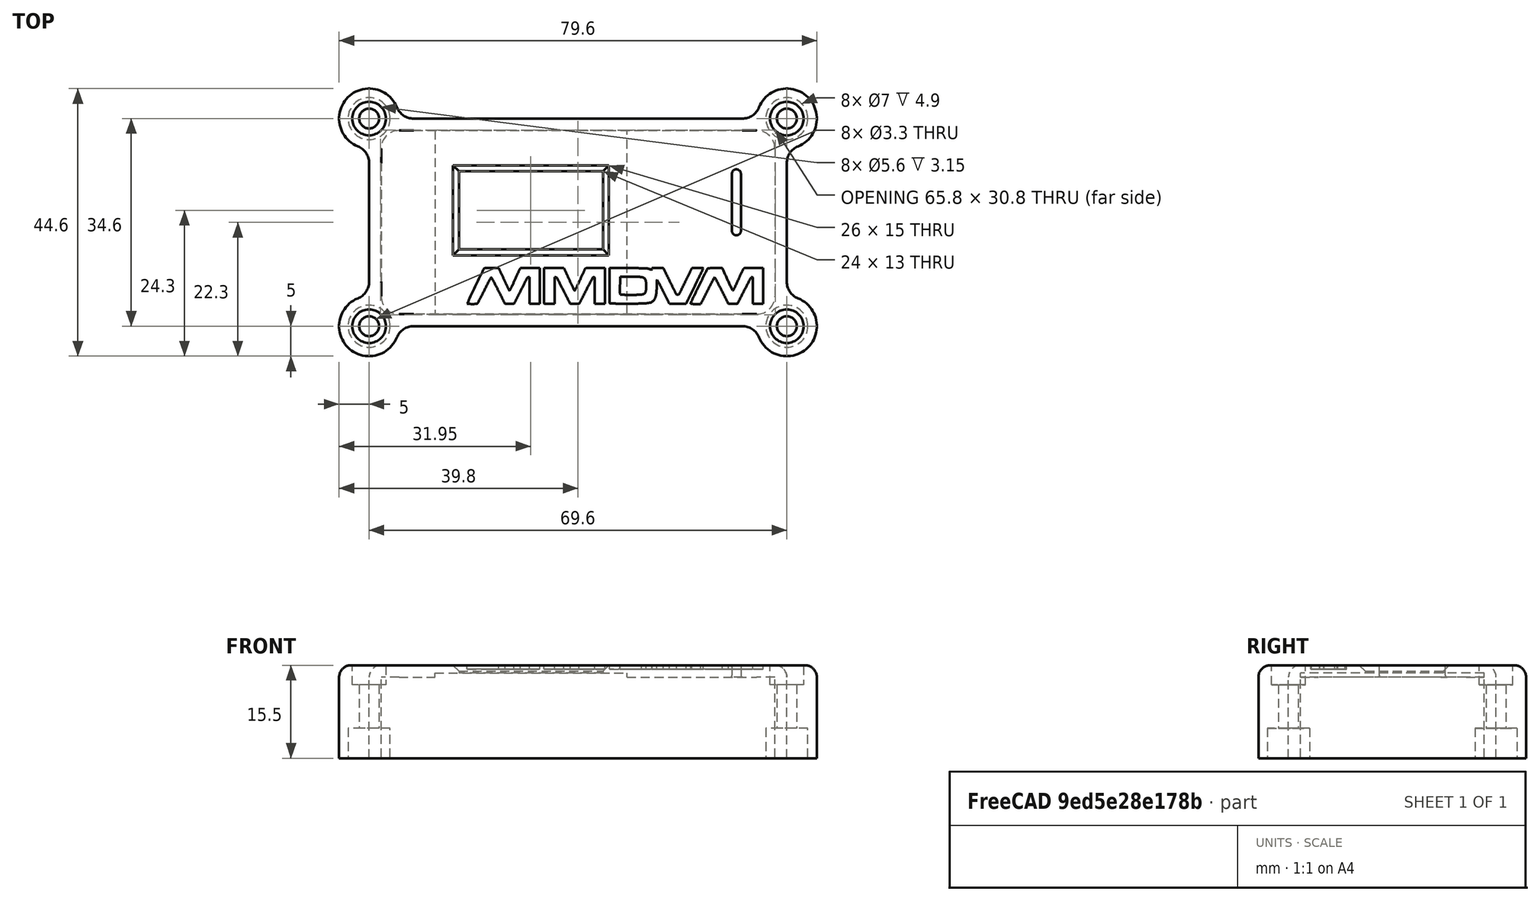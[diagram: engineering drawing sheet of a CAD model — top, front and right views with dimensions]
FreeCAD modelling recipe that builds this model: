
FCSTD DOCUMENT  (FreeCAD 0.18R13830 (Git))
Label: MMDVM_HS_Top-Screen-PCB-v1.2
License: CreativeCommons Attribution-NonCommercial-ShareAlike
LicenseURL: http://creativecommons.org/licenses/by-nc-sa/4.0/
objects: Sketcher::SketchObject×10, PartDesign::Pocket×6, Part::Feature×5, PartDesign::Fillet×4, Part::Cut×2, PartDesign::Pad×1, PartDesign::Chamfer×1, PartDesign::Hole×1, Part::MultiFuse×1, Part::FeaturePython×1, PartDesign::Body×1, Part::Extrusion×1, Mesh::Feature×1
note: 42 computed .brp shape members not serialized (recipe doc carries the construction recipe); baked Part::Feature solids carry a one-line shape summary decoded from their .brp

FEATURE [Sketcher::SketchObject] Sketch
  MapMode = 5
  Support = -> [XY_Plane]
  sketch-geometry (24):
    g0: LineSegment [constr] StartX=-32.5 StartY=15 StartZ=0 EndX=32.5 EndY=15 EndZ=0
    g1: LineSegment [constr] StartX=32.5 StartY=15 StartZ=0 EndX=32.5 EndY=-15 EndZ=0
    g2: LineSegment [constr] StartX=32.5 StartY=-15 StartZ=0 EndX=-32.5 EndY=-15 EndZ=0
    g3: LineSegment [constr] StartX=-32.5 StartY=-15 StartZ=0 EndX=-32.5 EndY=15 EndZ=0
    g4: LineSegment [constr] StartX=-29 StartY=11.5 StartZ=0 EndX=29 EndY=11.5 EndZ=0
    g5: LineSegment [constr] StartX=29 StartY=11.5 StartZ=0 EndX=29 EndY=-11.5 EndZ=0
    g6: LineSegment [constr] StartX=29 StartY=-11.5 StartZ=0 EndX=-29 EndY=-11.5 EndZ=0
    g7: LineSegment [constr] StartX=-29 StartY=-11.5 StartZ=0 EndX=-29 EndY=11.5 EndZ=0
    g8: Circle CenterX=-29 CenterY=11.5 CenterZ=0 NormalX=0 NormalY=0 NormalZ=1 AngleXU=0 Radius=1.375
    g9: Circle CenterX=29 CenterY=11.5 CenterZ=0 NormalX=0 NormalY=0 NormalZ=1 AngleXU=0 Radius=1.375
    g10: Circle CenterX=29 CenterY=-11.5 CenterZ=0 NormalX=0 NormalY=0 NormalZ=1 AngleXU=0 Radius=1.375
    g11: Circle CenterX=-29 CenterY=-11.5 CenterZ=0 NormalX=0 NormalY=0 NormalZ=1 AngleXU=0 Radius=1.375
    g12: LineSegment [constr] StartX=-29.5 StartY=12 StartZ=0 EndX=29.5 EndY=12 EndZ=0
    g13: LineSegment [constr] StartX=29.5 StartY=12 StartZ=0 EndX=29.5 EndY=-12 EndZ=0
    g14: LineSegment [constr] StartX=29.5 StartY=-12 StartZ=0 EndX=-29.5 EndY=-12 EndZ=0
    g15: LineSegment [constr] StartX=-29.5 StartY=-12 StartZ=0 EndX=-29.5 EndY=12 EndZ=0
    g16: ArcOfCircle CenterX=-29.5 CenterY=12 CenterZ=0 NormalX=0 NormalY=0 NormalZ=1 AngleXU=0 Radius=3 StartAngle=1.5708 EndAngle=3.1416
    g17: ArcOfCircle CenterX=29.5 CenterY=12 CenterZ=0 NormalX=0 NormalY=0 NormalZ=1 AngleXU=0 Radius=3 StartAngle=1.42077e-07 EndAngle=1.5708
    g18: ArcOfCircle CenterX=29.5 CenterY=-12 CenterZ=0 NormalX=0 NormalY=0 NormalZ=1 AngleXU=0 Radius=3 StartAngle=4.71239 EndAngle=6.28319
    g19: ArcOfCircle CenterX=-29.5 CenterY=-12 CenterZ=0 NormalX=0 NormalY=0 NormalZ=1 AngleXU=0 Radius=3 StartAngle=3.14159 EndAngle=4.71239
    g20: LineSegment StartX=-29.5 StartY=15 StartZ=0 EndX=29.5 EndY=15 EndZ=0
    g21: LineSegment StartX=32.5 StartY=12 StartZ=0 EndX=32.5 EndY=-12 EndZ=0
    g22: LineSegment StartX=29.5 StartY=-15 StartZ=0 EndX=-29.5 EndY=-15 EndZ=0
    g23: LineSegment StartX=-32.5 StartY=-12 StartZ=0 EndX=-32.5 EndY=12 EndZ=0
  constraints (68):
    c: Coincident(g0,g1)
    c: Coincident(g1,g2)
    c: Coincident(g2,g3)
    c: Coincident(g3,g0)
    c: Horizontal(g0)
    c: Horizontal(g2)
    c: Vertical(g1)
    c: Vertical(g3)
    c: DistanceX(g0,g0) = 65
    c: DistanceY(g1,g1) = 30
    c: Symmetric(g0,g0,g-2)
    c: Symmetric(g0,g1,g-1)
    c: Coincident(g4,g5)
    c: Coincident(g5,g6)
    c: Coincident(g6,g7)
    c: Coincident(g7,g4)
    c: Horizontal(g4)
    c: Horizontal(g6)
    c: Vertical(g5)
    c: Vertical(g7)
    c: DistanceX(g4,g4) = 58
    c: DistanceY(g5,g5) = 23
    c: Symmetric(g4,g5,g-1)
    c: Symmetric(g4,g4,g-2)
    c: Coincident(g8,g4)
    c: Coincident(g9,g4)
    c: Coincident(g10,g5)
    c: Coincident(g11,g6)
    c: Radius(g11) = 1.375
    c: Radius(g8) = 1.375
    c: Radius(g9) = 1.375
    c: Radius(g10) = 1.375
    c: Coincident(g12,g13)
    c: Coincident(g13,g14)
    c: Coincident(g14,g15)
    c: Coincident(g15,g12)
    c: Horizontal(g12)
    c: Horizontal(g14)
    c: Vertical(g13)
    c: Vertical(g15)
    c: DistanceX(g4,g12) = 0.5
    c: DistanceY(g4,g12) = 0.5
    c: DistanceY(g13,g5) = 0.5
    c: DistanceX(g14,g6) = 0.5
    c: Coincident(g16,g12)
    c: Radius(g16) = 3
    c: Coincident(g17,g12)
    c: Radius(g17) = 3
    c: Coincident(g18,g13)
    c: Radius(g18) = 3
    c: Coincident(g19,g14)
    c: Radius(g19) = 3
    c: PointOnObject(g16,g0)
    c: PointOnObject(g17,g1)
    c: PointOnObject(g18,g2)
    c: PointOnObject(g19,g3)
    c: Coincident(g20,g16)
    c: Horizontal(g20)
    c: Coincident(g20,g17)
    c: Coincident(g21,g17)
    c: Vertical(g21)
    c: Coincident(g18,g21)
    c: Coincident(g22,g18)
    c: Horizontal(g22)
    c: Coincident(g19,g22)
    c: Coincident(g23,g19)
    c: Vertical(g23)
    c: Coincident(g23,g16)
FEATURE [Sketcher::SketchObject] Sketch001
  MapMode = 5
  Support = -> [XY_Plane]
  expr: Constraints[8] = Sketch.Constraints[8]
  expr: Constraints[41] = Sketch.Constraints[41]
  expr: Constraints[9] = Sketch.Constraints[9]
  expr: Constraints[45] = Sketch.Constraints[45]
  expr: Constraints[43] = Sketch.Constraints[43]
  expr: Constraints[42] = Sketch.Constraints[42]
  expr: Constraints[20] = Sketch.Constraints[20]
  expr: Constraints[21] = Sketch.Constraints[21]
  expr: Constraints[28] = Sketch.Constraints[28]
  expr: Constraints[29] = Sketch.Constraints[29]
  expr: Constraints[30] = Sketch.Constraints[30]
  expr: Constraints[40] = Sketch.Constraints[40]
  expr: Constraints[31] = Sketch.Constraints[31]
  expr: Constraints[47] = Sketch.Constraints[47]
  expr: Constraints[49] = Sketch.Constraints[49]
  expr: Constraints[51] = Sketch.Constraints[51]
  sketch-geometry (64):
    g0: LineSegment [constr] StartX=-32.5 StartY=15 StartZ=0 EndX=32.5 EndY=15 EndZ=0
    g1: LineSegment [constr] StartX=32.5 StartY=15 StartZ=0 EndX=32.5 EndY=-15 EndZ=0
    g2: LineSegment [constr] StartX=32.5 StartY=-15 StartZ=0 EndX=-32.5 EndY=-15 EndZ=0
    g3: LineSegment [constr] StartX=-32.5 StartY=-15 StartZ=0 EndX=-32.5 EndY=15 EndZ=0
    g4: LineSegment [constr] StartX=-29 StartY=11.5 StartZ=0 EndX=29 EndY=11.5 EndZ=0
    g5: LineSegment [constr] StartX=29 StartY=11.5 StartZ=0 EndX=29 EndY=-11.5 EndZ=0
    g6: LineSegment [constr] StartX=29 StartY=-11.5 StartZ=0 EndX=-29 EndY=-11.5 EndZ=0
    g7: LineSegment [constr] StartX=-29 StartY=-11.5 StartZ=0 EndX=-29 EndY=11.5 EndZ=0
    g8: Circle [constr] CenterX=-29 CenterY=11.5 CenterZ=0 NormalX=0 NormalY=0 NormalZ=1 AngleXU=0 Radius=1.375
    g9: Circle [constr] CenterX=29 CenterY=11.5 CenterZ=0 NormalX=0 NormalY=0 NormalZ=1 AngleXU=0 Radius=1.375
    g10: Circle [constr] CenterX=29 CenterY=-11.5 CenterZ=0 NormalX=0 NormalY=0 NormalZ=1 AngleXU=0 Radius=1.375
    g11: Circle [constr] CenterX=-29 CenterY=-11.5 CenterZ=0 NormalX=0 NormalY=0 NormalZ=1 AngleXU=0 Radius=1.375
    g12: LineSegment [constr] StartX=-29.5 StartY=12 StartZ=0 EndX=29.5 EndY=12 EndZ=0
    g13: LineSegment [constr] StartX=29.5 StartY=12 StartZ=0 EndX=29.5 EndY=-12 EndZ=0
    g14: LineSegment [constr] StartX=29.5 StartY=-12 StartZ=0 EndX=-29.5 EndY=-12 EndZ=0
    g15: LineSegment [constr] StartX=-29.5 StartY=-12 StartZ=0 EndX=-29.5 EndY=12 EndZ=0
    g16: ArcOfCircle [constr] CenterX=-29.5 CenterY=12 CenterZ=0 NormalX=0 NormalY=0 NormalZ=1 AngleXU=0 Radius=3 StartAngle=1.5708 EndAngle=3.14159
    g17: ArcOfCircle [constr] CenterX=29.5 CenterY=12 CenterZ=0 NormalX=0 NormalY=0 NormalZ=1 AngleXU=0 Radius=3 StartAngle=2.8425e-08 EndAngle=1.5708
    g18: ArcOfCircle [constr] CenterX=29.5 CenterY=-12 CenterZ=0 NormalX=0 NormalY=0 NormalZ=1 AngleXU=0 Radius=3 StartAngle=4.71239 EndAngle=6.28319
    g19: ArcOfCircle [constr] CenterX=-29.5 CenterY=-12 CenterZ=0 NormalX=0 NormalY=0 NormalZ=1 AngleXU=0 Radius=3 StartAngle=3.14159 EndAngle=4.71239
    g20: LineSegment [constr] StartX=-29.5 StartY=15 StartZ=0 EndX=29.5 EndY=15 EndZ=0
    g21: LineSegment [constr] StartX=32.5 StartY=12 StartZ=0 EndX=32.5 EndY=-12 EndZ=0
    g22: LineSegment [constr] StartX=29.5 StartY=-15 StartZ=0 EndX=-29.5 EndY=-15 EndZ=0
    g23: LineSegment [constr] StartX=-32.5 StartY=-12 StartZ=0 EndX=-32.5 EndY=12 EndZ=0
    g24: ArcOfCircle [constr] CenterX=-29.5 CenterY=12 CenterZ=0 NormalX=0 NormalY=0 NormalZ=1 AngleXU=0 Radius=3.3 StartAngle=1.5708 EndAngle=3.14159
    g25: ArcOfCircle [constr] CenterX=29.5 CenterY=12 CenterZ=0 NormalX=0 NormalY=0 NormalZ=1 AngleXU=0 Radius=3.3 StartAngle=-2.2e-10 EndAngle=1.5708
    g26: ArcOfCircle [constr] CenterX=29.5 CenterY=-12 CenterZ=0 NormalX=0 NormalY=0 NormalZ=1 AngleXU=0 Radius=3.3 StartAngle=4.71239 EndAngle=6.28319
    g27: ArcOfCircle [constr] CenterX=-29.5 CenterY=-12 CenterZ=0 NormalX=0 NormalY=0 NormalZ=1 AngleXU=0 Radius=3.3 StartAngle=3.14159 EndAngle=4.71239
    g28: LineSegment [constr] StartX=-32.8 StartY=12 StartZ=0 EndX=-32.8 EndY=-12 EndZ=0
    g29: LineSegment [constr] StartX=-29.5 StartY=15.3 StartZ=0 EndX=29.5 EndY=15.3 EndZ=0
    g30: LineSegment [constr] StartX=32.8 StartY=12 StartZ=0 EndX=32.8 EndY=-12 EndZ=0
    g31: LineSegment [constr] StartX=29.5 StartY=-15.3 StartZ=0 EndX=-29.5 EndY=-15.3 EndZ=0
    g32: LineSegment [constr] StartX=-34.8 StartY=17.3 StartZ=0 EndX=34.8 EndY=17.3 EndZ=0
    g33: LineSegment [constr] StartX=34.8 StartY=17.3 StartZ=0 EndX=34.8 EndY=-17.3 EndZ=0
    g34: LineSegment [constr] StartX=34.8 StartY=-17.3 StartZ=0 EndX=-34.8 EndY=-17.3 EndZ=0
    g35: LineSegment [constr] StartX=-34.8 StartY=-17.3 StartZ=0 EndX=-34.8 EndY=17.3 EndZ=0
    g36: Circle [constr] CenterX=34.8 CenterY=17.3 CenterZ=0 NormalX=0 NormalY=0 NormalZ=1 AngleXU=0 Radius=5
    g37: Circle [constr] CenterX=34.8 CenterY=-17.3 CenterZ=0 NormalX=0 NormalY=0 NormalZ=1 AngleXU=0 Radius=5
    g38: Circle [constr] CenterX=-34.8 CenterY=-17.3 CenterZ=0 NormalX=0 NormalY=0 NormalZ=1 AngleXU=0 Radius=5
    g39: Circle [constr] CenterX=-34.8 CenterY=17.3 CenterZ=0 NormalX=0 NormalY=0 NormalZ=1 AngleXU=0 Radius=5
    g40: Circle [constr] CenterX=27.3838 CenterY=20.3 CenterZ=0 NormalX=0 NormalY=0 NormalZ=1 AngleXU=0 Radius=3
    g41: Circle [constr] CenterX=-27.3838 CenterY=20.3 CenterZ=0 NormalX=0 NormalY=0 NormalZ=1 AngleXU=0 Radius=3
    g42: Circle [constr] CenterX=-37.8 CenterY=9.8838 CenterZ=0 NormalX=0 NormalY=0 NormalZ=1 AngleXU=0 Radius=3
    g43: Circle [constr] CenterX=-37.8 CenterY=-9.8838 CenterZ=0 NormalX=0 NormalY=0 NormalZ=1 AngleXU=0 Radius=3
    g44: Circle [constr] CenterX=-27.3838 CenterY=-20.3 CenterZ=0 NormalX=0 NormalY=0 NormalZ=1 AngleXU=0 Radius=3
    g45: Circle [constr] CenterX=27.3838 CenterY=-20.3 CenterZ=0 NormalX=0 NormalY=0 NormalZ=1 AngleXU=0 Radius=3
    g46: Circle [constr] CenterX=37.8 CenterY=-9.8838 CenterZ=0 NormalX=0 NormalY=0 NormalZ=1 AngleXU=0 Radius=3
    g47: Circle [constr] CenterX=37.8 CenterY=9.8838 CenterZ=0 NormalX=0 NormalY=0 NormalZ=1 AngleXU=0 Radius=3
    g48: ArcOfCircle CenterX=34.8 CenterY=17.3 CenterZ=0 NormalX=0 NormalY=0 NormalZ=1 AngleXU=0 Radius=5 StartAngle=5.09679 EndAngle=9.04038
    g49: ArcOfCircle CenterX=27.3838 CenterY=20.3 CenterZ=0 NormalX=0 NormalY=0 NormalZ=1 AngleXU=0 Radius=3 StartAngle=4.71239 EndAngle=5.89879
    g50: ArcOfCircle CenterX=37.8 CenterY=9.8838 CenterZ=0 NormalX=0 NormalY=0 NormalZ=1 AngleXU=0 Radius=3 StartAngle=1.95519 EndAngle=3.14159
    g51: ArcOfCircle CenterX=37.8 CenterY=-9.8838 CenterZ=0 NormalX=0 NormalY=0 NormalZ=1 AngleXU=0 Radius=3 StartAngle=3.14159 EndAngle=4.32799
    g52: ArcOfCircle CenterX=34.8 CenterY=-17.3 CenterZ=0 NormalX=0 NormalY=0 NormalZ=1 AngleXU=0 Radius=5 StartAngle=3.52599 EndAngle=7.46958
    g53: ArcOfCircle CenterX=27.3838 CenterY=-20.3 CenterZ=0 NormalX=0 NormalY=0 NormalZ=1 AngleXU=0 Radius=3 StartAngle=0.384397 EndAngle=1.5708
    g54: ArcOfCircle CenterX=-27.3838 CenterY=-20.3 CenterZ=0 NormalX=0 NormalY=0 NormalZ=1 AngleXU=0 Radius=3 StartAngle=1.5708 EndAngle=2.7572
    g55: ArcOfCircle CenterX=-34.8 CenterY=-17.3 CenterZ=0 NormalX=0 NormalY=0 NormalZ=1 AngleXU=0 Radius=5 StartAngle=1.95519 EndAngle=5.89879
    g56: ArcOfCircle CenterX=-37.8 CenterY=-9.8838 CenterZ=0 NormalX=0 NormalY=0 NormalZ=1 AngleXU=0 Radius=3 StartAngle=5.09679 EndAngle=6.28319
    g57: ArcOfCircle CenterX=-37.8 CenterY=9.8838 CenterZ=0 NormalX=0 NormalY=0 NormalZ=1 AngleXU=0 Radius=3 StartAngle=6.28319 EndAngle=7.46958
    g58: ArcOfCircle CenterX=-34.8 CenterY=17.3 CenterZ=0 NormalX=0 NormalY=0 NormalZ=1 AngleXU=0 Radius=5 StartAngle=0.384397 EndAngle=4.32799
    g59: ArcOfCircle CenterX=-27.3838 CenterY=20.3 CenterZ=0 NormalX=0 NormalY=0 NormalZ=1 AngleXU=0 Radius=3 StartAngle=3.52599 EndAngle=4.71239
    g60: LineSegment StartX=-27.3838 StartY=17.3 StartZ=0 EndX=27.3838 EndY=17.3 EndZ=0
    g61: LineSegment StartX=34.8 StartY=9.8838 StartZ=0 EndX=34.8 EndY=-9.8838 EndZ=0
    g62: LineSegment StartX=27.3838 StartY=-17.3 StartZ=0 EndX=-27.3838 EndY=-17.3 EndZ=0
    g63: LineSegment StartX=-34.8 StartY=-9.8838 StartZ=0 EndX=-34.8 EndY=9.8838 EndZ=0
  constraints (184):
    c: Coincident(g0,g1)
    c: Coincident(g1,g2)
    c: Coincident(g2,g3)
    c: Coincident(g3,g0)
    c: Horizontal(g0)
    c: Horizontal(g2)
    c: Vertical(g1)
    c: Vertical(g3)
    c: DistanceX(g0,g0) = 65
    c: DistanceY(g1,g1) = 30
    c: Symmetric(g0,g0,g-2)
    c: Symmetric(g0,g1,g-1)
    c: Coincident(g4,g5)
    c: Coincident(g5,g6)
    c: Coincident(g6,g7)
    c: Coincident(g7,g4)
    c: Horizontal(g4)
    c: Horizontal(g6)
    c: Vertical(g5)
    c: Vertical(g7)
    c: DistanceX(g4,g4) = 58
    c: DistanceY(g5,g5) = 23
    c: Symmetric(g4,g5,g-1)
    c: Symmetric(g4,g4,g-2)
    c: Coincident(g8,g4)
    c: Coincident(g9,g4)
    c: Coincident(g10,g5)
    c: Coincident(g11,g6)
    c: Radius(g11) = 1.375
    c: Radius(g8) = 1.375
    c: Radius(g9) = 1.375
    c: Radius(g10) = 1.375
    c: Coincident(g12,g13)
    c: Coincident(g13,g14)
    c: Coincident(g14,g15)
    c: Coincident(g15,g12)
    c: Horizontal(g12)
    c: Horizontal(g14)
    c: Vertical(g13)
    c: Vertical(g15)
    c: DistanceX(g4,g12) = 0.5
    c: DistanceY(g4,g12) = 0.5
    c: DistanceY(g13,g5) = 0.5
    c: DistanceX(g14,g6) = 0.5
    c: Coincident(g16,g12)
    c: Radius(g16) = 3
    c: Coincident(g17,g12)
    c: Radius(g17) = 3
    c: Coincident(g18,g13)
    c: Radius(g18) = 3
    c: Coincident(g19,g14)
    c: Radius(g19) = 3
    c: PointOnObject(g16,g0)
    c: PointOnObject(g17,g1)
    c: PointOnObject(g18,g2)
    c: PointOnObject(g19,g3)
    c: Coincident(g20,g16)
    c: Horizontal(g20)
    c: Coincident(g20,g17)
    c: Coincident(g21,g17)
    c: Vertical(g21)
    c: Coincident(g18,g21)
    c: Coincident(g22,g18)
    c: Horizontal(g22)
    c: Coincident(g19,g22)
    c: Coincident(g23,g19)
    c: Vertical(g23)
    c: Coincident(g23,g16)
    c: Coincident(g24,g12)
    c: Radius(g24) = 3.3
    c: Coincident(g25,g12)
    c: Radius(g25) = 3.3
    c: Coincident(g26,g13)
    c: Radius(g26) = 3.3
    c: Coincident(g27,g14)
    c: Radius(g27) = 3.3
    c: Vertical(g28)
    c: DistanceX(g28,g2) = 0.3
    c: Coincident(g27,g28)
    c: Coincident(g28,g24)
    c: Horizontal(g29)
    c: DistanceY(g0,g29) = 0.3
    c: Coincident(g24,g29)
    c: Coincident(g25,g29)
    c: Vertical(g30)
    c: DistanceX(g0,g30) = 0.3
    c: Coincident(g25,g30)
    c: Coincident(g30,g26)
    c: Horizontal(g31)
    c: DistanceY(g31,g1) = 0.3
    c: Coincident(g31,g26)
    c: Coincident(g31,g27)
    c: Coincident(g32,g33)
    c: Coincident(g33,g34)
    c: Coincident(g34,g35)
    c: Coincident(g35,g32)
    c: Horizontal(g32)
    c: Horizontal(g34)
    c: Vertical(g33)
    c: Vertical(g35)
    c: DistanceY(g25,g32) = 2
    c: DistanceX(g25,g32) = 2
    c: DistanceY(g33,g26) = 2
    c: DistanceX(g34,g27) = 2
    c: Coincident(g36,g32)
    c: Coincident(g37,g33)
    c: Coincident(g38,g34)
    c: Coincident(g39,g32)
    c: Radius(g39) = 5
    c: Radius(g38) = 5
    c: Radius(g37) = 5
    c: Radius(g36) = 5
    c: Radius(g40) = 3
    c: Tangent(g40,g36)
    c: Tangent(g40,g32)
    c: Tangent(g47,g36)
    c: Radius(g47) = 3
    c: Tangent(g47,g33)
    c: Radius(g46) = 3
    c: Tangent(g46,g37)
    c: Tangent(g46,g33)
    c: Radius(g45) = 3
    c: Tangent(g45,g37)
    c: Tangent(g45,g34)
    c: Radius(g44) = 3
    c: Tangent(g44,g34)
    c: Tangent(g44,g38)
    c: Radius(g43) = 3
    c: Tangent(g43,g38)
    c: Tangent(g43,g35)
    c: Radius(g42) = 3
    c: Tangent(g42,g35)
    c: Tangent(g42,g39)
    c: Radius(g41) = 3
    c: Tangent(g41,g32)
    c: Tangent(g41,g39)
    c: Coincident(g48,g32)
    c: PointOnObject(g48,g36)
    c: Coincident(g49,g40)
    c: PointOnObject(g49,g40)
    c: Coincident(g50,g47)
    c: PointOnObject(g50,g47)
    c: Coincident(g51,g46)
    c: PointOnObject(g51,g46)
    c: Coincident(g52,g33)
    c: PointOnObject(g52,g37)
    c: Coincident(g53,g45)
    c: PointOnObject(g53,g45)
    c: Coincident(g54,g44)
    c: PointOnObject(g54,g44)
    c: Coincident(g55,g34)
    c: PointOnObject(g55,g38)
    c: Coincident(g56,g43)
    c: PointOnObject(g56,g43)
    c: Coincident(g57,g42)
    c: PointOnObject(g57,g42)
    c: Coincident(g58,g32)
    c: PointOnObject(g58,g39)
    c: Coincident(g59,g41)
    c: PointOnObject(g59,g41)
    c: Coincident(g49,g48)
    c: Coincident(g48,g50)
    c: Coincident(g51,g52)
    c: Coincident(g52,g53)
    c: Coincident(g54,g55)
    c: Coincident(g55,g56)
    c: Coincident(g57,g58)
    c: Coincident(g58,g59)
    c: PointOnObject(g60,g32)
    c: Horizontal(g60)
    c: PointOnObject(g61,g33)
    c: Vertical(g61)
    c: PointOnObject(g62,g34)
    c: Horizontal(g62)
    c: PointOnObject(g63,g35)
    c: Vertical(g63)
    c: Coincident(g59,g60)
    c: Coincident(g60,g49)
    c: Coincident(g50,g61)
    c: Coincident(g61,g51)
    c: Coincident(g53,g62)
    c: Coincident(g54,g62)
    c: Coincident(g56,g63)
    c: Coincident(g57,g63)
FEATURE [PartDesign::Pad] Pad
  Length = 15.5
  Length2 = 100
  Profile = -> Sketch001
  Type = 0
FEATURE [Sketcher::SketchObject] Sketch002
  ExternalGeometry = -> [Pad]
  MapMode = 5
  Placement = pos=(0,0,0) rot=(1,0,0;3.14159rad)
  Support = -> [Pad]
  sketch-geometry (4):
    g0: Circle CenterX=34.8 CenterY=17.3 CenterZ=0 NormalX=0 NormalY=0 NormalZ=1 AngleXU=0 Radius=3.5
    g1: Circle CenterX=34.8 CenterY=-17.3 CenterZ=0 NormalX=0 NormalY=0 NormalZ=1 AngleXU=0 Radius=3.5
    g2: Circle CenterX=-34.8 CenterY=-17.3 CenterZ=0 NormalX=0 NormalY=0 NormalZ=1 AngleXU=0 Radius=3.5
    g3: Circle CenterX=-34.8 CenterY=17.3 CenterZ=0 NormalX=0 NormalY=0 NormalZ=1 AngleXU=0 Radius=3.5
  constraints (8):
    c: Coincident(g0,g-3)
    c: Radius(g0) = 3.5
    c: Coincident(g1,g-6)
    c: Radius(g1) = 3.5
    c: Coincident(g2,g-5)
    c: Radius(g2) = 3.5
    c: Coincident(g3,g-4)
    c: Radius(g3) = 3.5
FEATURE [PartDesign::Pocket] Pocket
  BaseFeature = -> Pad
  Length = 5
  Length2 = 100
  Profile = -> Sketch002
  Type = 0
FEATURE [Sketcher::SketchObject] Sketch003
  MapMode = 5
  Placement = pos=(0,0,0) rot=(1,0,0;3.14159rad)
  Support = -> [Pocket]
  expr: Constraints[8] = Sketch.Constraints[8]
  expr: Constraints[39] = Sketch.Constraints[40]
  expr: Constraints[30] = Sketch.Constraints[31]
  expr: Constraints[27] = Sketch.Constraints[28]
  expr: Constraints[29] = Sketch.Constraints[30]
  expr: Constraints[28] = Sketch.Constraints[29]
  expr: Constraints[20] = -Sketch.Constraints[21]
  expr: Constraints[19] = Sketch.Constraints[20]
  expr: Constraints[42] = Sketch.Constraints[43]
  expr: Constraints[41] = -Sketch.Constraints[42]
  expr: Constraints[9] = -Sketch.Constraints[9]
  expr: Constraints[40] = -Sketch.Constraints[41]
  sketch-geometry (32):
    g0: LineSegment [constr] StartX=-32.5 StartY=-15 StartZ=0 EndX=32.5 EndY=-15 EndZ=0
    g1: LineSegment [constr] StartX=32.5 StartY=-15 StartZ=0 EndX=32.5 EndY=15 EndZ=0
    g2: LineSegment [constr] StartX=32.5 StartY=15 StartZ=0 EndX=-32.5 EndY=15 EndZ=0
    g3: LineSegment [constr] StartX=-32.5 StartY=15 StartZ=0 EndX=-32.5 EndY=-15 EndZ=0
    g4: LineSegment [constr] StartX=-29 StartY=-11.5 StartZ=0 EndX=29 EndY=-11.5 EndZ=0
    g5: LineSegment [constr] StartX=29 StartY=-11.5 StartZ=0 EndX=29 EndY=11.5 EndZ=0
    g6: LineSegment [constr] StartX=29 StartY=11.5 StartZ=0 EndX=-29 EndY=11.5 EndZ=0
    g7: LineSegment [constr] StartX=-29 StartY=11.5 StartZ=0 EndX=-29 EndY=-11.5 EndZ=0
    g8: Circle [constr] CenterX=-29 CenterY=-11.5 CenterZ=0 NormalX=0 NormalY=0 NormalZ=1 AngleXU=0 Radius=1.375
    g9: Circle [constr] CenterX=29 CenterY=-11.5 CenterZ=0 NormalX=0 NormalY=0 NormalZ=1 AngleXU=0 Radius=1.375
    g10: Circle [constr] CenterX=29 CenterY=11.5 CenterZ=0 NormalX=0 NormalY=0 NormalZ=1 AngleXU=0 Radius=1.375
    g11: Circle [constr] CenterX=-29 CenterY=11.5 CenterZ=0 NormalX=0 NormalY=0 NormalZ=1 AngleXU=0 Radius=1.375
    g12: LineSegment [constr] StartX=-29.5 StartY=-12 StartZ=0 EndX=29.5 EndY=-12 EndZ=0
    g13: LineSegment [constr] StartX=29.5 StartY=-12 StartZ=0 EndX=29.5 EndY=12 EndZ=0
    g14: LineSegment [constr] StartX=29.5 StartY=12 StartZ=0 EndX=-29.5 EndY=12 EndZ=0
    g15: LineSegment [constr] StartX=-29.5 StartY=12 StartZ=0 EndX=-29.5 EndY=-12 EndZ=0
    g16: LineSegment [constr] StartX=-29.5121 StartY=-15 StartZ=0 EndX=29.5 EndY=-15 EndZ=0
    g17: LineSegment [constr] StartX=32.5 StartY=-12 StartZ=0 EndX=32.5 EndY=12 EndZ=0
    g18: LineSegment [constr] StartX=29.5 StartY=15 StartZ=0 EndX=-29.5121 EndY=15 EndZ=0
    g19: LineSegment [constr] StartX=-32.5 StartY=12 StartZ=0 EndX=-32.5 EndY=-12 EndZ=0
    g20: ArcOfCircle [constr] CenterX=-29.5 CenterY=12 CenterZ=0 NormalX=0 NormalY=0 NormalZ=1 AngleXU=0 Radius=3.00002 StartAngle=1.57483 EndAngle=3.1416
    g21: ArcOfCircle [constr] CenterX=29.5 CenterY=12 CenterZ=0 NormalX=0 NormalY=0 NormalZ=1 AngleXU=0 Radius=3 StartAngle=6.28318 EndAngle=7.85399
    g22: ArcOfCircle [constr] CenterX=29.5 CenterY=-12 CenterZ=0 NormalX=0 NormalY=0 NormalZ=1 AngleXU=0 Radius=3 StartAngle=4.71238 EndAngle=6.28319
    g23: ArcOfCircle [constr] CenterX=-29.5 CenterY=-12 CenterZ=0 NormalX=0 NormalY=0 NormalZ=1 AngleXU=0 Radius=3.00002 StartAngle=3.14159 EndAngle=4.70836
    g24: LineSegment StartX=-29.8 StartY=15.3 StartZ=0 EndX=29.8 EndY=15.3 EndZ=0
    g25: LineSegment StartX=32.8 StartY=12.3 StartZ=0 EndX=32.8 EndY=-12.3 EndZ=0
    g26: LineSegment StartX=29.8 StartY=-15.3 StartZ=0 EndX=-29.8 EndY=-15.3 EndZ=0
    g27: LineSegment StartX=-32.8 StartY=-12.3 StartZ=0 EndX=-32.8 EndY=12.3 EndZ=0
    g28: ArcOfCircle CenterX=29.8 CenterY=12.3 CenterZ=0 NormalX=0 NormalY=0 NormalZ=1 AngleXU=0 Radius=3 StartAngle=0 EndAngle=1.5708
    g29: ArcOfCircle CenterX=29.8 CenterY=-12.3 CenterZ=0 NormalX=0 NormalY=0 NormalZ=1 AngleXU=0 Radius=3 StartAngle=4.71239 EndAngle=6.28319
    g30: ArcOfCircle CenterX=-29.8 CenterY=-12.3 CenterZ=0 NormalX=0 NormalY=0 NormalZ=1 AngleXU=0 Radius=3 StartAngle=3.14159 EndAngle=4.71239
    g31: ArcOfCircle CenterX=-29.8 CenterY=12.3 CenterZ=0 NormalX=0 NormalY=0 NormalZ=1 AngleXU=0 Radius=3 StartAngle=1.5708 EndAngle=3.14159
  constraints (83):
    c: Coincident(g0,g1)
    c: Coincident(g1,g2)
    c: Coincident(g2,g3)
    c: Coincident(g3,g0)
    c: Horizontal(g0)
    c: Horizontal(g2)
    c: Vertical(g1)
    c: Vertical(g3)
    c: DistanceX(g0,g0) = 65
    c: DistanceY(g1,g1) = -30
    c: Symmetric(g0,g0,g-2)
    c: Symmetric(g0,g1,g-1)
    c: Coincident(g4,g5)
    c: Coincident(g5,g6)
    c: Coincident(g6,g7)
    c: Horizontal(g4)
    c: Horizontal(g6)
    c: Vertical(g5)
    c: Vertical(g7)
    c: DistanceX(g4,g4) = 58
    c: DistanceY(g5,g5) = -23
    c: Symmetric(g4,g5,g-1)
    c: Symmetric(g4,g4,g-2)
    c: Coincident(g8,g4)
    c: Coincident(g9,g4)
    c: Coincident(g10,g5)
    c: Coincident(g11,g6)
    c: Radius(g11) = 1.375
    c: Radius(g8) = 1.375
    c: Radius(g9) = 1.375
    c: Radius(g10) = 1.375
    c: Coincident(g12,g13)
    c: Coincident(g13,g14)
    c: Coincident(g14,g15)
    c: Coincident(g15,g12)
    c: Horizontal(g12)
    c: Horizontal(g14)
    c: Vertical(g13)
    c: Vertical(g15)
    c: DistanceX(g4,g12) = 0.5
    c: DistanceY(g4,g12) = -0.5
    c: DistanceY(g13,g5) = -0.5
    c: DistanceX(g14,g6) = 0.5
    c: PointOnObject(g16,g0)
    c: PointOnObject(g17,g1)
    c: PointOnObject(g18,g2)
    c: PointOnObject(g19,g3)
    c: Horizontal(g16)
    c: Vertical(g17)
    c: Horizontal(g18)
    c: Vertical(g19)
    c: Coincident(g20,g14)
    c: Coincident(g20,g18)
    c: Coincident(g20,g19)
    c: Coincident(g21,g13)
    c: Coincident(g21,g17)
    c: Coincident(g21,g18)
    c: Coincident(g22,g12)
    c: Coincident(g22,g16)
    c: Coincident(g22,g17)
    c: Coincident(g23,g12)
    c: Coincident(g23,g19)
    c: Coincident(g23,g16)
    c: Horizontal(g24)
    c: Horizontal(g26)
    c: Vertical(g25)
    c: Vertical(g27)
    c: Tangent(g24,g28) = 1.5708
    c: Tangent(g25,g28) = 1.5708
    c: Tangent(g25,g29) = 1.5708
    c: Tangent(g26,g29) = 1.5708
    c: Tangent(g26,g30) = 1.5708
    c: Tangent(g27,g30) = 1.5708
    c: Tangent(g27,g31) = 1.5708
    c: Tangent(g24,g31) = 1.5708
    c: Radius(g31) = 3
    c: Radius(g28) = 3
    c: Radius(g29) = 3
    c: Radius(g30) = 3
    c: DistanceY(g1,g24) = 0.3
    c: DistanceX(g17,g25) = 0.3
    c: DistanceY(g26,g16) = 0.3
    c: DistanceX(g27,g19) = 0.3
FEATURE [PartDesign::Pocket] Pocket001
  BaseFeature = -> Pocket
  Length = 13.5
  Length2 = 100
  Profile = -> Sketch003
  Type = 0
FEATURE [Sketcher::SketchObject] Sketch004
  ExternalGeometry = -> [Pocket001]
  MapMode = 5
  Placement = pos=(0,0,15.5) rot=(0,0,1;0rad)
  Support = -> [Pocket001]
  sketch-geometry (32):
    g0: LineSegment StartX=-27.3838 StartY=17.3 StartZ=0 EndX=-31.8 EndY=17.3 EndZ=0
    g1: LineSegment StartX=-34.8 StartY=9.8838 StartZ=0 EndX=-34.8 EndY=14.3 EndZ=0
    g2: Circle [constr] CenterX=-31.8 CenterY=14.3 CenterZ=0 NormalX=0 NormalY=0 NormalZ=1 AngleXU=0 Radius=3
    g3: ArcOfCircle CenterX=-31.8 CenterY=14.3 CenterZ=0 NormalX=0 NormalY=0 NormalZ=1 AngleXU=0 Radius=3 StartAngle=1.5708 EndAngle=3.14159
    g4: LineSegment StartX=-41.7809 StartY=24.2149 StartZ=0 EndX=-27.3838 EndY=24.2149 EndZ=0
    g5: LineSegment StartX=-41.7809 StartY=9.8838 StartZ=0 EndX=-41.7809 EndY=24.2149 EndZ=0
    g6: LineSegment StartX=-27.3838 StartY=24.2149 StartZ=0 EndX=-27.3838 EndY=17.3 EndZ=0
    g7: LineSegment StartX=-41.7809 StartY=9.8838 StartZ=0 EndX=-34.8 EndY=9.8838 EndZ=0
    g8: LineSegment StartX=27.3838 StartY=17.3 StartZ=0 EndX=31.8 EndY=17.3 EndZ=0
    g9: LineSegment StartX=34.8 StartY=9.8838 StartZ=0 EndX=34.8 EndY=14.3 EndZ=0
    g10: Circle [constr] CenterX=31.8 CenterY=14.3 CenterZ=0 NormalX=0 NormalY=0 NormalZ=1 AngleXU=0 Radius=3
    g11: ArcOfCircle CenterX=31.8 CenterY=14.3 CenterZ=0 NormalX=0 NormalY=0 NormalZ=1 AngleXU=0 Radius=3 StartAngle=4.4834e-08 EndAngle=1.5708
    g12: LineSegment StartX=41.7622 StartY=24.6512 StartZ=0 EndX=27.3838 EndY=24.6512 EndZ=0
    g13: LineSegment StartX=41.7622 StartY=9.8838 StartZ=0 EndX=41.7622 EndY=24.6512 EndZ=0
    g14: LineSegment StartX=27.3838 StartY=24.6512 StartZ=0 EndX=27.3838 EndY=17.3 EndZ=0
    g15: LineSegment StartX=41.7622 StartY=9.8838 StartZ=0 EndX=34.8 EndY=9.8838 EndZ=0
    g16: LineSegment StartX=-34.8 StartY=-9.8838 StartZ=0 EndX=-34.8 EndY=-14.3 EndZ=0
    g17: LineSegment StartX=-27.3838 StartY=-17.3 StartZ=0 EndX=-31.8 EndY=-17.3 EndZ=0
    g18: Circle [constr] CenterX=-31.8 CenterY=-14.3 CenterZ=0 NormalX=0 NormalY=0 NormalZ=1 AngleXU=0 Radius=3
    g19: ArcOfCircle CenterX=-31.8 CenterY=-14.3 CenterZ=0 NormalX=0 NormalY=0 NormalZ=1 AngleXU=0 Radius=3 StartAngle=3.14159 EndAngle=4.71239
    g20: LineSegment StartX=-27.3838 StartY=-24.2044 StartZ=0 EndX=-41.4724 EndY=-24.2044 EndZ=0
    g21: LineSegment StartX=-41.4724 StartY=-24.2044 StartZ=0 EndX=-41.4724 EndY=-9.8838 EndZ=0
    g22: LineSegment StartX=-41.4724 StartY=-9.8838 StartZ=0 EndX=-34.8 EndY=-9.8838 EndZ=0
    g23: LineSegment StartX=-27.3838 StartY=-24.2044 StartZ=0 EndX=-27.3838 EndY=-17.3 EndZ=0
    g24: LineSegment StartX=34.8 StartY=-9.8838 StartZ=0 EndX=34.8 EndY=-14.3 EndZ=0
    g25: LineSegment StartX=27.3838 StartY=-17.3 StartZ=0 EndX=31.8 EndY=-17.3 EndZ=0
    g26: Circle [constr] CenterX=31.8 CenterY=-14.3 CenterZ=0 NormalX=0 NormalY=0 NormalZ=1 AngleXU=0 Radius=3
    g27: ArcOfCircle CenterX=31.8 CenterY=-14.3 CenterZ=0 NormalX=0 NormalY=0 NormalZ=1 AngleXU=0 Radius=3 StartAngle=4.71239 EndAngle=6.28319
    g28: LineSegment StartX=41.5436 StartY=-23.6904 StartZ=0 EndX=27.3838 EndY=-23.6904 EndZ=0
    g29: LineSegment StartX=41.5436 StartY=-9.8838 StartZ=0 EndX=41.5436 EndY=-23.6904 EndZ=0
    g30: LineSegment StartX=41.5436 StartY=-9.8838 StartZ=0 EndX=34.8 EndY=-9.8838 EndZ=0
    g31: LineSegment StartX=27.3838 StartY=-23.6904 StartZ=0 EndX=27.3838 EndY=-17.3 EndZ=0
  constraints (88):
    c: PointOnObject(g0,g-3)
    c: Horizontal(g0)
    c: PointOnObject(g1,g-6)
    c: Vertical(g1)
    c: Radius(g2) = 3
    c: Tangent(g2,g0)
    c: Tangent(g2,g1)
    c: Coincident(g3,g2)
    c: PointOnObject(g3,g2)
    c: Coincident(g3,g1)
    c: Coincident(g3,g0)
    c: Coincident(g5,g4)
    c: Horizontal(g4)
    c: Vertical(g5)
    c: Coincident(g6,g4)
    c: Vertical(g6)
    c: Coincident(g7,g5)
    c: Horizontal(g7)
    c: Coincident(g7,g1)
    c: Coincident(g6,g0)
    c: PointOnObject(g8,g-3)
    c: Horizontal(g8)
    c: PointOnObject(g9,g-4)
    c: Vertical(g9)
    c: Radius(g10) = 3
    c: Tangent(g10,g8)
    c: Tangent(g10,g9)
    c: Coincident(g11,g10)
    c: PointOnObject(g11,g10)
    c: Coincident(g11,g8)
    c: Coincident(g11,g9)
    c: Coincident(g13,g12)
    c: Horizontal(g12)
    c: Vertical(g13)
    c: Coincident(g14,g12)
    c: Vertical(g14)
    c: Coincident(g15,g13)
    c: Horizontal(g15)
    c: Coincident(g15,g9)
    c: Coincident(g14,g8)
    c: PointOnObject(g16,g-6)
    c: Vertical(g16)
    c: PointOnObject(g17,g-5)
    c: Horizontal(g17)
    c: Radius(g18) = 3
    c: Tangent(g18,g16)
    c: Tangent(g18,g17)
    c: Coincident(g19,g18)
    c: PointOnObject(g19,g18)
    c: Coincident(g19,g17)
    c: Coincident(g19,g16)
    c: Coincident(g20,g21)
    c: Horizontal(g20)
    c: Vertical(g21)
    c: Coincident(g22,g21)
    c: Horizontal(g22)
    c: Coincident(g23,g20)
    c: Vertical(g23)
    c: Coincident(g23,g17)
    c: Coincident(g22,g16)
    c: PointOnObject(g24,g-4)
    c: Vertical(g24)
    c: PointOnObject(g25,g-5)
    c: Horizontal(g25)
    c: Radius(g26) = 3
    c: Tangent(g26,g24)
    c: Tangent(g26,g25)
    c: Coincident(g27,g26)
    c: PointOnObject(g27,g26)
    c: Coincident(g27,g24)
    c: Coincident(g27,g25)
    c: Coincident(g29,g28)
    c: Horizontal(g28)
    c: Vertical(g29)
    c: Coincident(g30,g29)
    c: Horizontal(g30)
    c: Coincident(g31,g28)
    c: Vertical(g31)
    c: Coincident(g31,g25)
    c: Coincident(g30,g24)
    c: Coincident(g0,g-3)
    c: Coincident(g1,g-6)
    c: Coincident(g-6,g16)
    c: Coincident(g17,g-5)
    c: Coincident(g-5,g25)
    c: Coincident(g-4,g24)
    c: Coincident(g9,g-4)
    c: Coincident(g8,g-3)
FEATURE [Sketcher::SketchObject] Sketch005
  ExternalGeometry = -> [Pocket001,Sketch]
  MapMode = 5
  Placement = pos=(0,0,15.5) rot=(0,0,1;0rad)
  Support = -> [Pocket001]
  sketch-geometry (10):
    g0: LineSegment [constr] StartX=-27.35 StartY=31.2328 StartZ=0 EndX=-27.35 EndY=-27.0552 EndZ=0
    g1: LineSegment [constr] StartX=-45.4064 StartY=-0.9 StartZ=0 EndX=40.4454 EndY=-0.9 EndZ=0
    g2: Circle [constr] CenterX=-27.35 CenterY=-0.9 CenterZ=0 NormalX=0 NormalY=0 NormalZ=1 AngleXU=0 Radius=6.2
    g3: LineSegment StartX=-19.85 StartY=8.5 StartZ=0 EndX=4.15 EndY=8.5 EndZ=0
    g4: LineSegment StartX=4.15 StartY=8.5 StartZ=0 EndX=4.15 EndY=-4.5 EndZ=0
    g5: LineSegment StartX=4.15 StartY=-4.5 StartZ=0 EndX=-19.85 EndY=-4.5 EndZ=0
    g6: LineSegment StartX=-19.85 StartY=-4.5 StartZ=0 EndX=-19.85 EndY=8.5 EndZ=0
    g7: LineSegment [constr] StartX=-29 StartY=24.9491 StartZ=0 EndX=-29 EndY=-20.674 EndZ=0
    g8: LineSegment [constr] StartX=-44.8443 StartY=11.5 StartZ=0 EndX=14.9752 EndY=11.5 EndZ=0
    g9: Circle [constr] CenterX=-27.35 CenterY=-0.9 CenterZ=0 NormalX=0 NormalY=0 NormalZ=1 AngleXU=0 Radius=2
  constraints (21):
    c: Coincident(g5,g6)
    c: Coincident(g3,g6)
    c: Coincident(g4,g5)
    c: Coincident(g3,g4)
    c: DistanceX(g3,g3) = 24
    c: DistanceY(g4,g4) = 13
    c: Vertical(g7)
    c: Horizontal(g8)
    c: PointOnObject(g-4,g8)
    c: PointOnObject(g-4,g7)
    c: PointOnObject(g2,g0)
    c: PointOnObject(g2,g1)
    c: DistanceX(g7,g0) = 1.65
    c: DistanceX(g7,g3) = 9.15
    c: DistanceY(g3,g-4) = 3
    c: DistanceY(g1,g8) = 12.4
    c: Vertical(g0)
    c: Horizontal(g1)
    c: Radius(g2) = 6.2
    c: Coincident(g9,g2)
    c: Radius(g9) = 2
FEATURE [PartDesign::Pocket] Pocket002
  BaseFeature = -> Pocket001
  Length = 5
  Length2 = 100
  Profile = -> Sketch005
  Type = 0
FEATURE [Sketcher::SketchObject] Sketch006
  ExternalGeometry = -> [Pocket002]
  MapMode = 5
  Placement = pos=(0,0,13.5) rot=(1,0,0;3.14159rad)
  Support = -> [Pocket002]
  sketch-geometry (4):
    g0: LineSegment StartX=-23.85 StartY=15.3 StartZ=0 EndX=8.15 EndY=15.3 EndZ=0
    g1: LineSegment StartX=8.15 StartY=15.3 StartZ=0 EndX=8.15 EndY=-15.3 EndZ=0
    g2: LineSegment StartX=8.15 StartY=-15.3 StartZ=0 EndX=-23.85 EndY=-15.3 EndZ=0
    g3: LineSegment StartX=-23.85 StartY=-15.3 StartZ=0 EndX=-23.85 EndY=15.3 EndZ=0
FEATURE [PartDesign::Pocket] Pocket003
  BaseFeature = -> Pocket002
  Length = 0.7
  Length2 = 100
  Profile = -> Sketch006
  Type = 0
FEATURE [PartDesign::Fillet] Fillet
  Base = -> Pocket003 [Edge38]
  BaseFeature = -> Pocket003
  Radius = 2
FEATURE [PartDesign::Chamfer] Chamfer
  Base = -> Fillet [Edge60,Edge59,Edge58,Edge57]
  BaseFeature = -> Fillet
  Size = 1
FEATURE [Sketcher::SketchObject] Sketch007
  MapMode = 5
  Placement = pos=(0,0,15.5) rot=(0,0,1;0rad)
  sketch-geometry (4):
    g0: Circle CenterX=34.8 CenterY=17.3 CenterZ=0 NormalX=0 NormalY=0 NormalZ=1 AngleXU=0 Radius=2.63102
    g1: Circle CenterX=-34.8 CenterY=17.3 CenterZ=0 NormalX=0 NormalY=0 NormalZ=1 AngleXU=0 Radius=2.66333
    g2: Circle CenterX=-34.8 CenterY=-17.3 CenterZ=0 NormalX=0 NormalY=0 NormalZ=1 AngleXU=0 Radius=2.82775
    g3: Circle CenterX=34.8 CenterY=-17.3 CenterZ=0 NormalX=0 NormalY=0 NormalZ=1 AngleXU=0 Radius=2.89107
FEATURE [PartDesign::Hole] Hole
  BaseFeature = -> Chamfer
  Depth = 20
  DepthType = 1
  Diameter = 3.3
  DrillPoint = 1
  DrillPointAngle = 118
  HoleCutCountersinkAngle = 90
  HoleCutDepth = 0
  HoleCutDiameter = 3
  HoleCutType = 0
  ModelActualThread = false
  Profile = -> Sketch007
  Tapered = false
  TaperedAngle = 90
  ThreadAngle = 60
  ThreadClass = 0
  ThreadCutOffInner = 0.0433013
  ThreadCutOffOuter = 0.0866025
  ThreadDirection = 0
  ThreadFit = 0
  ThreadPitch = 0.4
  ThreadSize = 3
  ThreadType = 1
  Threaded = false
FEATURE [Part::Feature] path76
  shape: bbox 67.53 x 33.36 x 2e-07 mm, 1 faces, 0 solids (baked)
FEATURE [Part::Feature] path76001
  shape: bbox 56.51 x 33.36 x 2e-07 mm, 1 faces, 0 solids (baked)
FEATURE [Part::Feature] path76002
  shape: bbox 67.23 x 33.39 x 2e-07 mm, 1 faces, 0 solids (baked)
FEATURE [Part::Feature] path76003
  shape: bbox 86.8 x 33.05 x 2e-07 mm, 1 faces, 0 solids (baked)
FEATURE [Part::Feature] path76004
  shape: bbox 24.36 x 17.06 x 2e-07 mm, 1 faces, 0 solids (baked)
FEATURE [Part::Cut] Cut
  Base = -> path76003
  Tool = -> path76004
FEATURE [Part::MultiFuse] Fusion
  Shapes = -> [path76,path76001,path76002,Cut]
FEATURE [Part::FeaturePython] Scale001  # Draft clone (typed FeaturePython)
  Fuse = false
  Objects = -> [Fusion]
  Placement = pos=(-20,0,14.85) rot=(0,0,1;0rad)
  Scale = (0.18,0.18,0.18)
FEATURE [Sketcher::SketchObject] Sketch010
  ExternalGeometry = -> [Hole]
  MapMode = 5
  Placement = pos=(0,0,15.5) rot=(0,0,1;0rad)
  Support = -> [Hole]
  sketch-geometry (4):
    g0: Circle CenterX=34.8 CenterY=17.3 CenterZ=0 NormalX=0 NormalY=0 NormalZ=1 AngleXU=0 Radius=2.8
    g1: Circle CenterX=34.8 CenterY=-17.3 CenterZ=0 NormalX=0 NormalY=0 NormalZ=1 AngleXU=0 Radius=2.8
    g2: Circle CenterX=-34.8 CenterY=-17.3 CenterZ=0 NormalX=0 NormalY=0 NormalZ=1 AngleXU=0 Radius=2.8
    g3: Circle CenterX=-34.8 CenterY=17.3 CenterZ=0 NormalX=0 NormalY=0 NormalZ=1 AngleXU=0 Radius=2.8
  constraints (8):
    c: Coincident(g0,g-3)
    c: Coincident(g1,g-6)
    c: Coincident(g2,g-5)
    c: Coincident(g3,g-4)
    c: Radius(g3) = 2.8
    c: Radius(g0) = 2.8
    c: Radius(g1) = 2.8
    c: Radius(g2) = 2.8
FEATURE [PartDesign::Pocket] Pocket006
  BaseFeature = -> Hole
  Length = 3.3
  Length2 = 100
  Profile = -> Sketch010
  Type = 0
FEATURE [PartDesign::Fillet] Fillet002
  Base = -> Pocket006 [Edge20,Edge19,Edge18,Edge17]
  BaseFeature = -> Pocket006
  Radius = 0.15
FEATURE [Sketcher::SketchObject] Sketch009
  MapMode = 5
  Placement = pos=(0,0,15.5) rot=(0,0,1;0rad)
  Support = -> [Fillet002]
  expr: Constraints[7] = Sketch.Constraints[9]
  expr: Constraints[40] = Sketch.Constraints[42]
  expr: Constraints[18] = Sketch.Constraints[20]
  expr: Constraints[19] = Sketch.Constraints[21]
  expr: Constraints[29] = Sketch.Constraints[31]
  expr: Constraints[27] = Sketch.Constraints[29]
  expr: Constraints[28] = Sketch.Constraints[30]
  expr: Constraints[26] = Sketch.Constraints[28]
  expr: Constraints[6] = Sketch.Constraints[8]
  expr: Constraints[38] = Sketch.Constraints[40]
  expr: Constraints[47] = Sketch.Constraints[49]
  expr: Constraints[39] = Sketch.Constraints[41]
  expr: Constraints[49] = Sketch.Constraints[51]
  expr: Constraints[45] = Sketch.Constraints[47]
  expr: Constraints[43] = Sketch.Constraints[45]
  expr: Constraints[41] = Sketch.Constraints[43]
  sketch-geometry (34):
    g0: LineSegment [constr] StartX=-32.5 StartY=15 StartZ=0 EndX=32.5 EndY=15 EndZ=0
    g1: LineSegment [constr] StartX=32.5 StartY=15 StartZ=0 EndX=32.5 EndY=-15 EndZ=0
    g2: LineSegment [constr] StartX=32.5 StartY=-15 StartZ=0 EndX=-32.5 EndY=-15 EndZ=0
    g3: LineSegment [constr] StartX=-32.5 StartY=-15 StartZ=0 EndX=-32.5 EndY=15 EndZ=0
    g4: LineSegment [constr] StartX=-29 StartY=11.5 StartZ=0 EndX=29 EndY=11.5 EndZ=0
    g5: LineSegment [constr] StartX=29 StartY=11.5 StartZ=0 EndX=29 EndY=-11.5 EndZ=0
    g6: LineSegment [constr] StartX=29 StartY=-11.5 StartZ=0 EndX=-29 EndY=-11.5 EndZ=0
    g7: LineSegment [constr] StartX=-29 StartY=-11.5 StartZ=0 EndX=-29 EndY=11.5 EndZ=0
    g8: Circle [constr] CenterX=-29 CenterY=11.5 CenterZ=0 NormalX=0 NormalY=0 NormalZ=1 AngleXU=0 Radius=1.375
    g9: Circle [constr] CenterX=29 CenterY=11.5 CenterZ=0 NormalX=0 NormalY=0 NormalZ=1 AngleXU=0 Radius=1.375
    g10: Circle [constr] CenterX=29 CenterY=-11.5 CenterZ=0 NormalX=0 NormalY=0 NormalZ=1 AngleXU=0 Radius=1.375
    g11: Circle [constr] CenterX=-29 CenterY=-11.5 CenterZ=0 NormalX=0 NormalY=0 NormalZ=1 AngleXU=0 Radius=1.375
    g12: LineSegment [constr] StartX=-29.5 StartY=12 StartZ=0 EndX=29.5 EndY=12 EndZ=0
    g13: LineSegment [constr] StartX=29.5 StartY=12 StartZ=0 EndX=29.5 EndY=-12 EndZ=0
    g14: LineSegment [constr] StartX=29.5 StartY=-12 StartZ=0 EndX=-29.5 EndY=-12 EndZ=0
    g15: LineSegment [constr] StartX=-29.5 StartY=-12 StartZ=0 EndX=-29.5 EndY=12 EndZ=0
    g16: ArcOfCircle [constr] CenterX=-29.5 CenterY=12 CenterZ=0 NormalX=0 NormalY=0 NormalZ=1 AngleXU=0 Radius=3 StartAngle=1.5708 EndAngle=3.14159
    g17: ArcOfCircle [constr] CenterX=29.5 CenterY=12 CenterZ=0 NormalX=0 NormalY=0 NormalZ=1 AngleXU=0 Radius=3 StartAngle=3.9602e-08 EndAngle=1.5708
    g18: ArcOfCircle [constr] CenterX=29.5 CenterY=-12 CenterZ=0 NormalX=0 NormalY=0 NormalZ=1 AngleXU=0 Radius=3 StartAngle=4.71239 EndAngle=6.28319
    g19: ArcOfCircle [constr] CenterX=-29.5 CenterY=-12 CenterZ=0 NormalX=0 NormalY=0 NormalZ=1 AngleXU=0 Radius=3 StartAngle=3.14159 EndAngle=4.71239
    g20: LineSegment [constr] StartX=-29.5 StartY=15 StartZ=0 EndX=29.5 EndY=15 EndZ=0
    g21: LineSegment [constr] StartX=32.5 StartY=12 StartZ=0 EndX=32.5 EndY=-12 EndZ=0
    g22: LineSegment [constr] StartX=29.5 StartY=-15 StartZ=0 EndX=-29.5 EndY=-15 EndZ=0
    g23: LineSegment [constr] StartX=-32.5 StartY=-12 StartZ=0 EndX=-32.5 EndY=12 EndZ=0
    g24: LineSegment [constr] StartX=26.4 StartY=27.403 StartZ=0 EndX=26.4 EndY=-26.3119 EndZ=0
    g25: ArcOfCircle CenterX=26.4 CenterY=8.09 CenterZ=0 NormalX=0 NormalY=0 NormalZ=1 AngleXU=0 Radius=0.75 StartAngle=0 EndAngle=3.14159
    g26: ArcOfCircle CenterX=26.4 CenterY=-1.41 CenterZ=0 NormalX=0 NormalY=0 NormalZ=1 AngleXU=0 Radius=0.75 StartAngle=3.14159 EndAngle=6.28319
    g27: LineSegment StartX=25.65 StartY=8.09 StartZ=0 EndX=25.65 EndY=-1.41 EndZ=0
    g28: LineSegment StartX=27.15 StartY=8.09 StartZ=0 EndX=27.15 EndY=-1.41 EndZ=0
    g29: LineSegment [constr] StartX=36.6897 StartY=3.34 StartZ=0 EndX=15.0074 EndY=3.34 EndZ=0
    g30: LineSegment [constr] StartX=25.4202 StartY=8.84 StartZ=0 EndX=27.4202 EndY=8.84 EndZ=0
    g31: LineSegment [constr] StartX=27.4202 StartY=8.84 StartZ=0 EndX=27.4202 EndY=-2.16 EndZ=0
    g32: LineSegment [constr] StartX=27.4202 StartY=-2.16 StartZ=0 EndX=25.4202 EndY=-2.16 EndZ=0
    g33: LineSegment [constr] StartX=25.4202 StartY=-2.16 StartZ=0 EndX=25.4202 EndY=8.84 EndZ=0
  constraints (91):
    c: Coincident(g0,g1)
    c: Coincident(g1,g2)
    c: Coincident(g2,g3)
    c: Coincident(g3,g0)
    c: Horizontal(g2)
    c: Vertical(g3)
    c: DistanceX(g0,g0) = 65
    c: DistanceY(g1,g1) = 30
    c: Symmetric(g0,g0,g-2)
    c: Symmetric(g0,g1,g-1)
    c: Coincident(g4,g5)
    c: Coincident(g5,g6)
    c: Coincident(g6,g7)
    c: Coincident(g7,g4)
    c: Horizontal(g4)
    c: Horizontal(g6)
    c: Vertical(g5)
    c: Vertical(g7)
    c: DistanceX(g4,g4) = 58
    c: DistanceY(g5,g5) = 23
    c: Symmetric(g4,g5,g-1)
    c: Symmetric(g4,g4,g-2)
    c: Coincident(g8,g4)
    c: Coincident(g9,g4)
    c: Coincident(g10,g5)
    c: Coincident(g11,g6)
    c: Radius(g11) = 1.375
    c: Radius(g8) = 1.375
    c: Radius(g9) = 1.375
    c: Radius(g10) = 1.375
    c: Coincident(g12,g13)
    c: Coincident(g13,g14)
    c: Coincident(g14,g15)
    c: Coincident(g15,g12)
    c: Horizontal(g12)
    c: Horizontal(g14)
    c: Vertical(g13)
    c: Vertical(g15)
    c: DistanceX(g4,g12) = 0.5
    c: DistanceY(g4,g12) = 0.5
    c: DistanceY(g13,g5) = 0.5
    c: DistanceX(g14,g6) = 0.5
    c: Coincident(g16,g12)
    c: Radius(g16) = 3
    c: Coincident(g17,g12)
    c: Radius(g17) = 3
    c: Coincident(g18,g13)
    c: Radius(g18) = 3
    c: Coincident(g19,g14)
    c: Radius(g19) = 3
    c: PointOnObject(g16,g0)
    c: PointOnObject(g17,g1)
    c: PointOnObject(g18,g2)
    c: PointOnObject(g19,g3)
    c: Coincident(g20,g16)
    c: Horizontal(g20)
    c: Coincident(g20,g17)
    c: Coincident(g21,g17)
    c: Vertical(g21)
    c: Coincident(g18,g21)
    c: Coincident(g22,g18)
    c: Horizontal(g22)
    c: Coincident(g19,g22)
    c: Coincident(g23,g19)
    c: Vertical(g23)
    c: Coincident(g23,g16)
    c: Vertical(g24)
    c: DistanceX(g24,g4) = 2.6
    c: Tangent(g25,g28) = 1.5708
    c: Tangent(g25,g27) = -1.5708
    c: Tangent(g27,g26) = -1.5708
    c: Tangent(g28,g26) = 1.5708
    c: Vertical(g27)
    c: Equal(g25,g26)
    c: PointOnObject(g25,g24)
    c: DistanceX(g26,g26) = 1.5
    c: Horizontal(g29)
    c: DistanceY(g29,g4) = 8.16
    c: Coincident(g30,g31)
    c: Coincident(g31,g32)
    c: Coincident(g32,g33)
    c: Coincident(g33,g30)
    c: Horizontal(g30)
    c: Horizontal(g32)
    c: Vertical(g31)
    c: Vertical(g33)
    c: DistanceY(g33,g33) = 11
    c: DistanceY(g29,g30) = 5.5
    c: DistanceX(g30,g30) = 2
    c: DistanceY(g26,g25) = 9.5
    c: Symmetric(g25,g26,g29)
FEATURE [PartDesign::Pocket] Pocket005
  BaseFeature = -> Fillet002
  Length = 5
  Length2 = 100
  Profile = -> Sketch009
  Type = 2
FEATURE [PartDesign::Fillet] Fillet003
  Base = -> Pocket005 [Edge21,Edge70]
  BaseFeature = -> Pocket005
  Radius = 0.3
FEATURE [PartDesign::Fillet] Fillet004
  Base = -> Fillet003 [Edge159,Edge149,Edge160,Edge158,Edge157]
  BaseFeature = -> Fillet003
  Radius = 0.1
FEATURE [PartDesign::Body] Body
  Group = -> [Sketch,Sketch001,Pad,Sketch002,Pocket,Sketch003,Pocket001,Sketch004,Sketch005,Pocket002,Sketch006,Pocket003,Fillet,Chamfer,Sketch007,Hole,Pocket006,Fillet002,Sketch009,Pocket005,Fillet003,Sketch010,Fillet004]
  Origin = -> Origin
  Tip = -> Fillet004
FEATURE [Part::Extrusion] Extrude
  Base = -> Scale001
  Dir = (0,0,1)
  DirMode = 0
  FaceMakerClass = Part::FaceMakerBullseye
  LengthFwd = 5
  LengthRev = 0
  Solid = false
  Symmetric = false
FEATURE [Part::Cut] Cut001
  Base = -> Fillet004
  Tool = -> Extrude
FEATURE [Mesh::Feature] Mesh  label="Cut001 (Meshed)"
